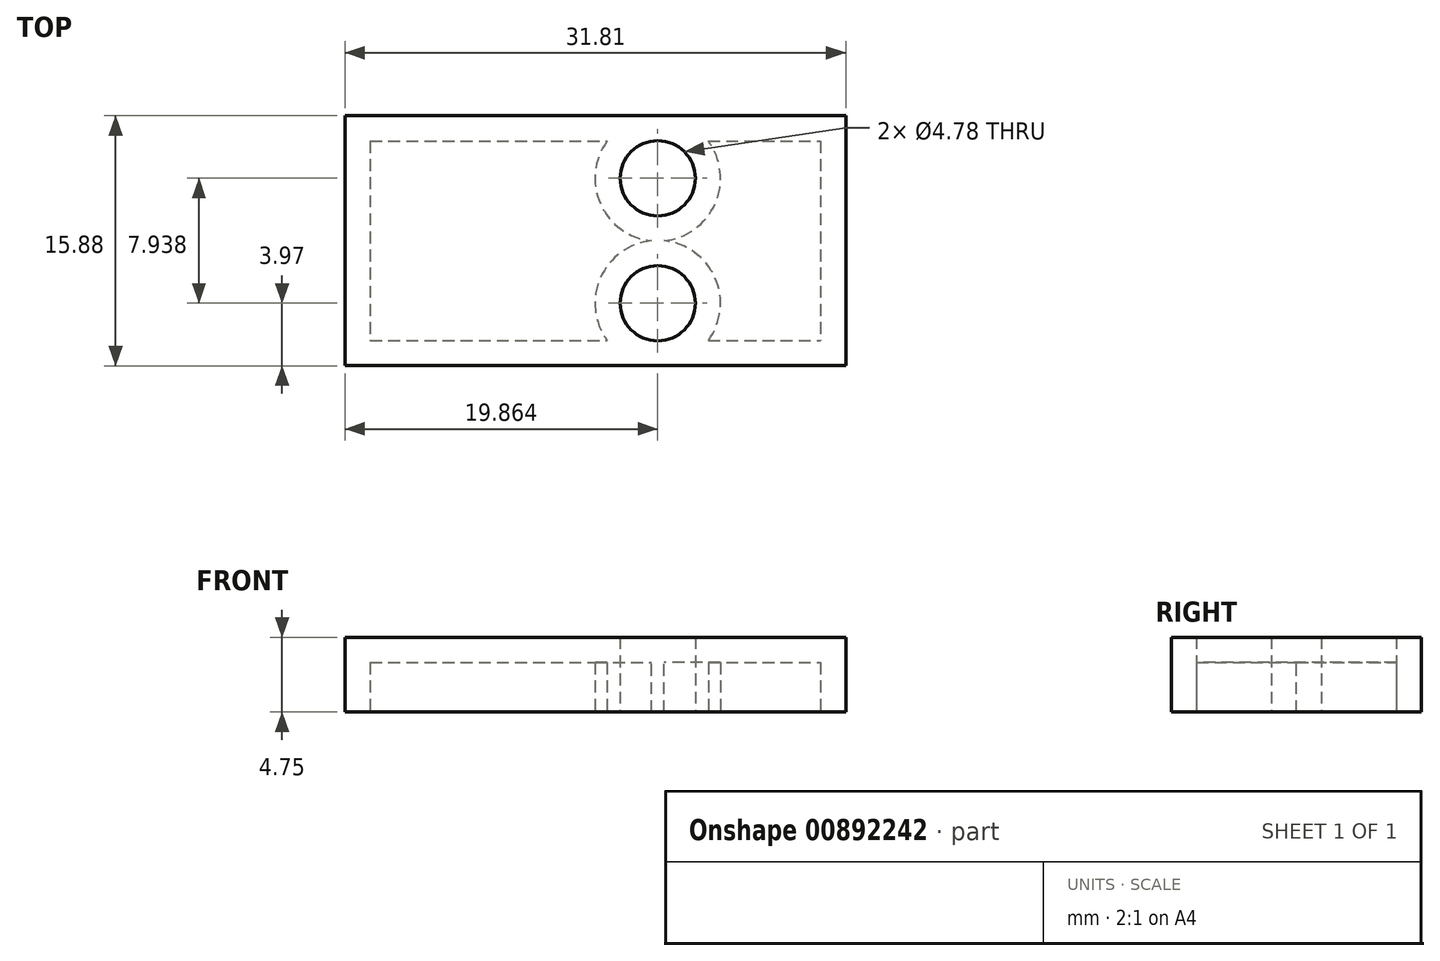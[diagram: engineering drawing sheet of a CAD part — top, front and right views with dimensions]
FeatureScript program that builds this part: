
annotation { "Feature Type Name" : "Feature", "Feature Type Description" : "" }
export const myFeature = defineFeature(function(context is Context, id is Id, definition is map)
    precondition{}
    {
        {
            var Q0;
            Q0=qCreatedBy(makeId("Top.planeOp"),FACE);
            var sketch = newSketch(context, id + "F0", { "sketchPlane" : qUnion([Q0])});
            skLineSegment(sketch, "E0.bottom", {"start": v(-38.8, 8.6) * mm, "end": v(-7, 8.6) * mm});
            skLineSegment(sketch, "E0.top", {"start": v(-38.8, -7.28) * mm, "end": v(-7, -7.28) * mm});
            skLineSegment(sketch, "E0.left", {"start": v(-38.8, 8.6) * mm, "end": v(-38.8, -7.28) * mm});
            skLineSegment(sketch, "E0.right", {"start": v(-7, 8.6) * mm, "end": v(-7, -7.28) * mm});
            skLineSegment(sketch, "E1", {"start": v(-38.8, 0.66) * mm, "end": v(-7, 0.66) * mm});
            skLineSegment(sketch, "E2", {"start": v(-7, 8.6) * mm, "end": v(-7, 0.66) * mm});
            skLineSegment(sketch, "E3", {"start": v(-7, 0.66) * mm, "end": v(-7, -7.28) * mm});
            skLineSegment(sketch, "E4", {"start": v(-38.8, 8.6) * mm, "end": v(-38.8, 0.66) * mm});
            skLineSegment(sketch, "E5", {"start": v(-38.8, -7.28) * mm, "end": v(-38.8, 0.66) * mm});
            skLineSegment(sketch, "E6", {"start": v(-7, -3.31) * mm, "end": v(-38.8, -3.31) * mm});
            skLineSegment(sketch, "E7", {"start": v(-38.8, -3.31) * mm, "end": v(-38.8, 4.63) * mm});
            skLineSegment(sketch, "E8", {"start": v(-38.8, 4.63) * mm, "end": v(-7, 4.63) * mm});
            skCircle(sketch, "E9", {"center": v(-34.85, 4.63) * mm, "radius": 2.39 * mm});
            skCircle(sketch, "E10.1.0.0", {"center": v(-26.9, 4.63) * mm, "radius": 2.39 * mm});
            skCircle(sketch, "E10.2.0.0", {"center": v(-18.95, 4.63) * mm, "radius": 2.39 * mm});
            skCircle(sketch, "E10.3.0.0", {"center": v(-11, 4.63) * mm, "radius": 2.39 * mm});
            skLineSegment(sketch, "E10.direction1", {"start": v(-34.85, 4.63) * mm, "end": v(-26.9, 4.63) * mm, "construction": true});
            skCircle(sketch, "E11.MirrorC", {"center": v(-34.85, -3.31) * mm, "radius": 2.39 * mm});
            skCircle(sketch, "E12.MirrorC", {"center": v(-26.9, -3.31) * mm, "radius": 2.39 * mm});
            skCircle(sketch, "E13.MirrorC", {"center": v(-18.95, -3.31) * mm, "radius": 2.39 * mm});
            skCircle(sketch, "E14.MirrorC", {"center": v(-11, -3.31) * mm, "radius": 2.39 * mm});
            skSolve(sketch);
        }
        {
            var Q0;
            {var subQ10=sQuery(id+"F0.wireOp",EDGE,"E0.bottom");Q0=makeQuery(id+"F0.imprint","IMPRINT",FACE,{"disambiguationData":[TD([[makeQuery(id+"F0.imprint","IMPRINT",EDGE,{"derivedFrom":subQ10}),-1.0]])]});}
            var Q1;
            {var subQ6=sQuery(id+"F0.wireOp",EDGE,"E1");Q1=makeQuery(id+"F0.imprint","IMPRINT",FACE,{"disambiguationData":[TD([[makeQuery(id+"F0.imprint","IMPRINT",EDGE,{"derivedFrom":subQ6}),1.0]])]});}
            var Q2;
            {var subQ12=sQuery(id+"F0.wireOp",EDGE,"E0.top");Q2=makeQuery(id+"F0.imprint","IMPRINT",FACE,{"disambiguationData":[TD([[makeQuery(id+"F0.imprint","IMPRINT",EDGE,{"derivedFrom":subQ12}),1.0]])]});}
            var Q3;
            {var subQ15=sQuery(id+"F0.wireOp",EDGE,"E1");Q3=makeQuery(id+"F0.imprint","IMPRINT",FACE,{"disambiguationData":[TD([[makeQuery(id+"F0.imprint","IMPRINT",EDGE,{"derivedFrom":subQ15}),-1.0]])]});}
            extrude(context, id + "F1", {"entities" : qUnion([Q0, Q1, Q2, Q3]), "depth" : 3.17 * mm, "offsetDistance" : 25.4 * mm});
        }
        {
            var Q0;
            {var subQ0=sQuery(id+"F0.wireOp",EDGE,"E9");var subQ1=sQuery(id+"F0.wireOp",EDGE,"E8");var subQ2=makeQuery(id+"F0.imprint","INTERSECT",VERTEX,{"disambiguationData":[OD(0.0)],"derivedFrom":[subQ1,subQ0]});Q0=makeQuery(id+"F0.imprint","IMPRINT",FACE,{"disambiguationData":[TD([[makeQuery(id+"F0.imprint","IMPRINT",EDGE,{"disambiguationData":[TD([[subQ2,-1.0]])],"derivedFrom":subQ1}),-1.0]])]});}
            var Q1;
            {var subQ0=sQuery(id+"F0.wireOp",EDGE,"E9");var subQ1=sQuery(id+"F0.wireOp",EDGE,"E8");var subQ2=makeQuery(id+"F0.imprint","INTERSECT",VERTEX,{"disambiguationData":[OD(0.0)],"derivedFrom":[subQ1,subQ0]});Q1=makeQuery(id+"F0.imprint","IMPRINT",FACE,{"disambiguationData":[TD([[makeQuery(id+"F0.imprint","IMPRINT",EDGE,{"disambiguationData":[TD([[subQ2,-1.0]])],"derivedFrom":subQ1}),1.0]])]});}
            var Q2;
            {var subQ0=sQuery(id+"F0.wireOp",EDGE,"E11.MirrorC");var subQ1=sQuery(id+"F0.wireOp",EDGE,"E6");var subQ2=makeQuery(id+"F0.imprint","INTERSECT",VERTEX,{"disambiguationData":[OD(0.0)],"derivedFrom":[subQ1,subQ0]});Q2=makeQuery(id+"F0.imprint","IMPRINT",FACE,{"disambiguationData":[TD([[makeQuery(id+"F0.imprint","IMPRINT",EDGE,{"disambiguationData":[TD([[subQ2,-1.0]])],"derivedFrom":subQ1}),-1.0]])]});}
            var Q3;
            {var subQ0=sQuery(id+"F0.wireOp",EDGE,"E11.MirrorC");var subQ1=sQuery(id+"F0.wireOp",EDGE,"E6");var subQ2=makeQuery(id+"F0.imprint","INTERSECT",VERTEX,{"disambiguationData":[OD(0.0)],"derivedFrom":[subQ1,subQ0]});Q3=makeQuery(id+"F0.imprint","IMPRINT",FACE,{"disambiguationData":[TD([[makeQuery(id+"F0.imprint","IMPRINT",EDGE,{"disambiguationData":[TD([[subQ2,-1.0]])],"derivedFrom":subQ1}),1.0]])]});}
            var Q4;
            {var subQ0=sQuery(id+"F0.wireOp",EDGE,"E12.MirrorC");var subQ1=sQuery(id+"F0.wireOp",EDGE,"E6");var subQ2=makeQuery(id+"F0.imprint","INTERSECT",VERTEX,{"disambiguationData":[OD(0.0)],"derivedFrom":[subQ1,subQ0]});Q4=makeQuery(id+"F0.imprint","IMPRINT",FACE,{"disambiguationData":[TD([[makeQuery(id+"F0.imprint","IMPRINT",EDGE,{"disambiguationData":[TD([[subQ2,1.0]])],"derivedFrom":subQ1}),1.0]])]});}
            var Q5;
            {var subQ0=sQuery(id+"F0.wireOp",EDGE,"E12.MirrorC");var subQ1=sQuery(id+"F0.wireOp",EDGE,"E6");var subQ2=makeQuery(id+"F0.imprint","INTERSECT",VERTEX,{"disambiguationData":[OD(0.0)],"derivedFrom":[subQ1,subQ0]});Q5=makeQuery(id+"F0.imprint","IMPRINT",FACE,{"disambiguationData":[TD([[makeQuery(id+"F0.imprint","IMPRINT",EDGE,{"disambiguationData":[TD([[subQ2,1.0]])],"derivedFrom":subQ1}),-1.0]])]});}
            var Q6;
            {var subQ0=sQuery(id+"F0.wireOp",EDGE,"E10.1.0.0");var subQ1=sQuery(id+"F0.wireOp",EDGE,"E8");var subQ2=makeQuery(id+"F0.imprint","INTERSECT",VERTEX,{"disambiguationData":[OD(0.0)],"derivedFrom":[subQ1,subQ0]});Q6=makeQuery(id+"F0.imprint","IMPRINT",FACE,{"disambiguationData":[TD([[makeQuery(id+"F0.imprint","IMPRINT",EDGE,{"disambiguationData":[TD([[subQ2,-1.0]])],"derivedFrom":subQ1}),-1.0]])]});}
            var Q7;
            {var subQ0=sQuery(id+"F0.wireOp",EDGE,"E10.1.0.0");var subQ1=sQuery(id+"F0.wireOp",EDGE,"E8");var subQ2=makeQuery(id+"F0.imprint","INTERSECT",VERTEX,{"disambiguationData":[OD(0.0)],"derivedFrom":[subQ1,subQ0]});Q7=makeQuery(id+"F0.imprint","IMPRINT",FACE,{"disambiguationData":[TD([[makeQuery(id+"F0.imprint","IMPRINT",EDGE,{"disambiguationData":[TD([[subQ2,-1.0]])],"derivedFrom":subQ1}),1.0]])]});}
            var Q8;
            {var subQ0=sQuery(id+"F0.wireOp",EDGE,"E13.MirrorC");var subQ1=sQuery(id+"F0.wireOp",EDGE,"E6");var subQ2=makeQuery(id+"F0.imprint","INTERSECT",VERTEX,{"disambiguationData":[OD(0.0)],"derivedFrom":[subQ1,subQ0]});Q8=makeQuery(id+"F0.imprint","IMPRINT",FACE,{"disambiguationData":[TD([[makeQuery(id+"F0.imprint","IMPRINT",EDGE,{"disambiguationData":[TD([[subQ2,-1.0]])],"derivedFrom":subQ1}),1.0]])]});}
            var Q9;
            {var subQ0=sQuery(id+"F0.wireOp",EDGE,"E13.MirrorC");var subQ1=sQuery(id+"F0.wireOp",EDGE,"E6");var subQ2=makeQuery(id+"F0.imprint","INTERSECT",VERTEX,{"disambiguationData":[OD(0.0)],"derivedFrom":[subQ1,subQ0]});Q9=makeQuery(id+"F0.imprint","IMPRINT",FACE,{"disambiguationData":[TD([[makeQuery(id+"F0.imprint","IMPRINT",EDGE,{"disambiguationData":[TD([[subQ2,-1.0]])],"derivedFrom":subQ1}),-1.0]])]});}
            var Q10;
            {var subQ0=sQuery(id+"F0.wireOp",EDGE,"E10.2.0.0");var subQ1=sQuery(id+"F0.wireOp",EDGE,"E8");var subQ2=makeQuery(id+"F0.imprint","INTERSECT",VERTEX,{"disambiguationData":[OD(0.0)],"derivedFrom":[subQ1,subQ0]});Q10=makeQuery(id+"F0.imprint","IMPRINT",FACE,{"disambiguationData":[TD([[makeQuery(id+"F0.imprint","IMPRINT",EDGE,{"disambiguationData":[TD([[subQ2,1.0]])],"derivedFrom":subQ1}),1.0]])]});}
            var Q11;
            {var subQ0=sQuery(id+"F0.wireOp",EDGE,"E10.2.0.0");var subQ1=sQuery(id+"F0.wireOp",EDGE,"E8");var subQ2=makeQuery(id+"F0.imprint","INTERSECT",VERTEX,{"disambiguationData":[OD(0.0)],"derivedFrom":[subQ1,subQ0]});Q11=makeQuery(id+"F0.imprint","IMPRINT",FACE,{"disambiguationData":[TD([[makeQuery(id+"F0.imprint","IMPRINT",EDGE,{"disambiguationData":[TD([[subQ2,1.0]])],"derivedFrom":subQ1}),-1.0]])]});}
            var Q12;
            {var subQ0=sQuery(id+"F0.wireOp",EDGE,"E14.MirrorC");var subQ1=sQuery(id+"F0.wireOp",EDGE,"E6");var subQ2=makeQuery(id+"F0.imprint","INTERSECT",VERTEX,{"disambiguationData":[OD(0.0)],"derivedFrom":[subQ1,subQ0]});Q12=makeQuery(id+"F0.imprint","IMPRINT",FACE,{"disambiguationData":[TD([[makeQuery(id+"F0.imprint","IMPRINT",EDGE,{"disambiguationData":[TD([[subQ2,1.0]])],"derivedFrom":subQ1}),-1.0]])]});}
            var Q13;
            {var subQ0=sQuery(id+"F0.wireOp",EDGE,"E14.MirrorC");var subQ1=sQuery(id+"F0.wireOp",EDGE,"E6");var subQ2=makeQuery(id+"F0.imprint","INTERSECT",VERTEX,{"disambiguationData":[OD(0.0)],"derivedFrom":[subQ1,subQ0]});Q13=makeQuery(id+"F0.imprint","IMPRINT",FACE,{"disambiguationData":[TD([[makeQuery(id+"F0.imprint","IMPRINT",EDGE,{"disambiguationData":[TD([[subQ2,1.0]])],"derivedFrom":subQ1}),1.0]])]});}
            var Q14;
            {var subQ0=sQuery(id+"F0.wireOp",EDGE,"E10.3.0.0");var subQ1=sQuery(id+"F0.wireOp",EDGE,"E8");var subQ2=makeQuery(id+"F0.imprint","INTERSECT",VERTEX,{"disambiguationData":[OD(0.0)],"derivedFrom":[subQ1,subQ0]});Q14=makeQuery(id+"F0.imprint","IMPRINT",FACE,{"disambiguationData":[TD([[makeQuery(id+"F0.imprint","IMPRINT",EDGE,{"disambiguationData":[TD([[subQ2,-1.0]])],"derivedFrom":subQ1}),-1.0]])]});}
            var Q15;
            {var subQ0=sQuery(id+"F0.wireOp",EDGE,"E10.3.0.0");var subQ1=sQuery(id+"F0.wireOp",EDGE,"E8");var subQ2=makeQuery(id+"F0.imprint","INTERSECT",VERTEX,{"disambiguationData":[OD(0.0)],"derivedFrom":[subQ1,subQ0]});Q15=makeQuery(id+"F0.imprint","IMPRINT",FACE,{"disambiguationData":[TD([[makeQuery(id+"F0.imprint","IMPRINT",EDGE,{"disambiguationData":[TD([[subQ2,-1.0]])],"derivedFrom":subQ1}),1.0]])]});}
            extrude(context, id + "F2", {"entities" : qUnion([Q0, Q1, Q2, Q3, Q4, Q5, Q6, Q7, Q8, Q9, Q10, Q11, Q12, Q13, Q14, Q15]), "operationType" : NewBodyOperationType.ADD, "depth" : 4.75 * mm, "offsetDistance" : 25.4 * mm});
        }
        {
            var Q0;
            {var subQ0=sQuery(id+"F0.wireOp",EDGE,"E14.MirrorC");var subQ1=sQuery(id+"F0.wireOp",EDGE,"E13.MirrorC");var subQ2=sQuery(id+"F0.wireOp",EDGE,"E12.MirrorC");var subQ3=sQuery(id+"F0.wireOp",EDGE,"E11.MirrorC");var subQ4=sQuery(id+"F0.wireOp",EDGE,"E10.3.0.0");var subQ5=sQuery(id+"F0.wireOp",EDGE,"E10.2.0.0");var subQ6=sQuery(id+"F0.wireOp",EDGE,"E10.1.0.0");var subQ7=sQuery(id+"F0.wireOp",EDGE,"E9");Q0=makeQuery(id+"F2.boolean.opBoolean","MERGE",FACE,{"derivedFrom":[makeQuery(id+"F1.opExtrude","CAP_FACE",FACE,{"disambiguationData":[OSD([sQuery(id+"F0.wireOp",EDGE,"E0.bottom"),sQuery(id+"F0.wireOp",EDGE,"E0.top"),sQuery(id+"F0.wireOp",EDGE,"E0.left"),sQuery(id+"F0.wireOp",EDGE,"E0.right"),subQ7,subQ6,subQ5,subQ4,subQ3,subQ2,subQ1,subQ0])],"isStart":true}),makeQuery(id+"F2.opExtrude","CAP_FACE",FACE,{"disambiguationData":[OSD([subQ7])],"isStart":true}),makeQuery(id+"F2.opExtrude","CAP_FACE",FACE,{"disambiguationData":[OSD([subQ6])],"isStart":true}),makeQuery(id+"F2.opExtrude","CAP_FACE",FACE,{"disambiguationData":[OSD([subQ5])],"isStart":true}),makeQuery(id+"F2.opExtrude","CAP_FACE",FACE,{"disambiguationData":[OSD([subQ4])],"isStart":true}),makeQuery(id+"F2.opExtrude","CAP_FACE",FACE,{"disambiguationData":[OSD([subQ3])],"isStart":true}),makeQuery(id+"F2.opExtrude","CAP_FACE",FACE,{"disambiguationData":[OSD([subQ2])],"isStart":true}),makeQuery(id+"F2.opExtrude","CAP_FACE",FACE,{"disambiguationData":[OSD([subQ1])],"isStart":true}),makeQuery(id+"F2.opExtrude","CAP_FACE",FACE,{"disambiguationData":[OSD([subQ0])],"isStart":true})]});}
            shell(context, id + "F3", {"entities" : qUnion([Q0]), "thickness" : 1.6 * mm});
        }
    });
